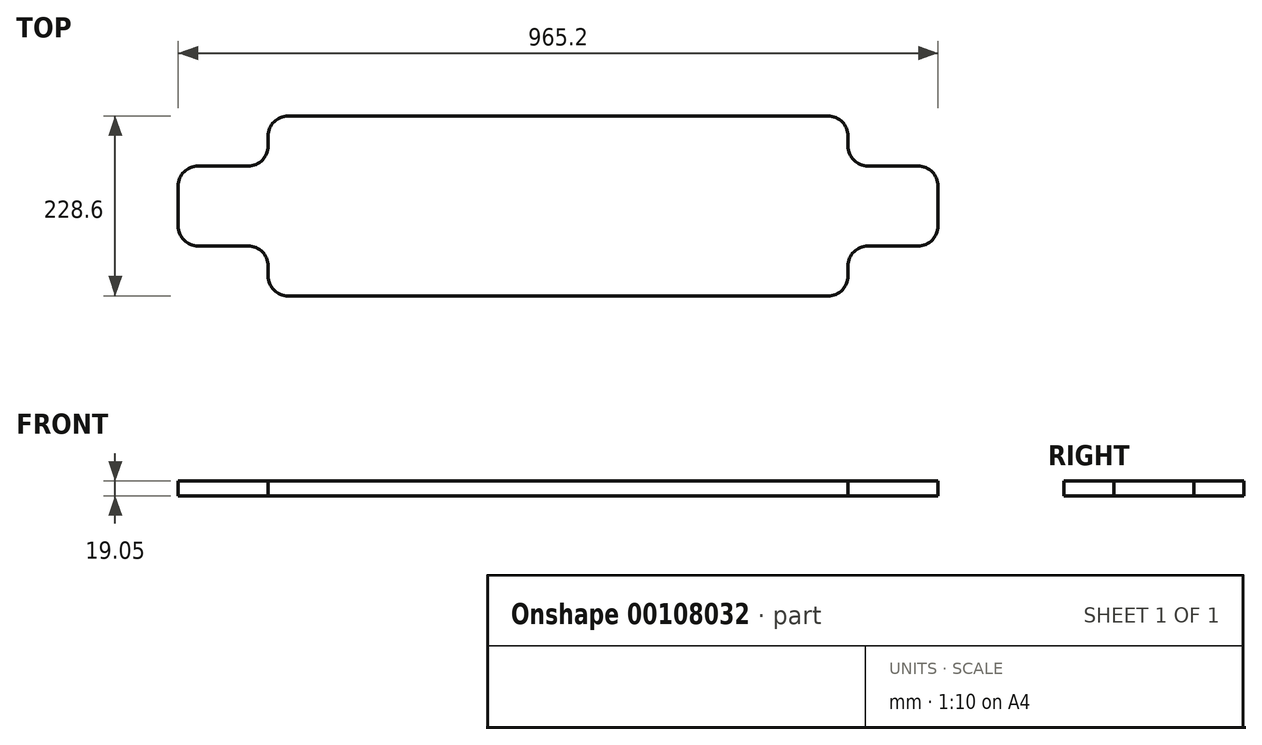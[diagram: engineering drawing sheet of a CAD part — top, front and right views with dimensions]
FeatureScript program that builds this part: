
annotation { "Feature Type Name" : "Feature", "Feature Type Description" : "" }
export const myFeature = defineFeature(function(context is Context, id is Id, definition is map)
    precondition{}
    {
        {
            var Q0;
            Q0=qCreatedBy(makeId("Top.planeOp"),FACE);
            var sketch = newSketch(context, id + "F0", { "sketchPlane" : qUnion([Q0])});
            skLineSegment(sketch, "E0", {"start": v(-342.9, 114.3) * mm, "end": v(342.9, 114.3) * mm});
            skLineSegment(sketch, "E1", {"start": v(368.3, 88.9) * mm, "end": v(368.3, 76.2) * mm});
            skLineSegment(sketch, "E2", {"start": v(393.7, 50.8) * mm, "end": v(457.2, 50.8) * mm});
            skLineSegment(sketch, "E3", {"start": v(482.6, 25.4) * mm, "end": v(482.6, -25.4) * mm});
            skLineSegment(sketch, "E4", {"start": v(457.2, -50.8) * mm, "end": v(393.7, -50.8) * mm});
            skLineSegment(sketch, "E5", {"start": v(368.3, -76.2) * mm, "end": v(368.3, -88.9) * mm});
            skLineSegment(sketch, "E6", {"start": v(342.9, -114.3) * mm, "end": v(-342.9, -114.3) * mm});
            skLineSegment(sketch, "E7", {"start": v(-368.3, -88.9) * mm, "end": v(-368.3, -76.2) * mm});
            skLineSegment(sketch, "E8", {"start": v(-393.7, -50.8) * mm, "end": v(-457.2, -50.8) * mm});
            skLineSegment(sketch, "E9", {"start": v(-482.6, -25.4) * mm, "end": v(-482.6, 25.4) * mm});
            skLineSegment(sketch, "E10", {"start": v(-457.2, 50.8) * mm, "end": v(-393.7, 50.8) * mm});
            skLineSegment(sketch, "E11", {"start": v(-368.3, 76.2) * mm, "end": v(-368.3, 88.9) * mm});
            skLineSegment(sketch, "E12", {"start": v(-368.3, 114.3) * mm, "end": v(368.3, -114.3) * mm, "construction": true});
            skPoint(sketch, "E13", {"position": v(0, 0) * mm});
            skPoint(sketch, "E14.visualSharp", {"position": v(-368.3, 50.8) * mm});
            skArc(sketch, "E14.filletArc", {"start": v(-393.7, 50.8) * mm, "mid": v(-375.74, 58.24) * mm, "end": v(-368.3, 76.2) * mm});
            skPoint(sketch, "E15.visualSharp", {"position": v(-482.6, 50.8) * mm});
            skArc(sketch, "E15.filletArc", {"start": v(-457.2, 50.8) * mm, "mid": v(-475.16, 43.36) * mm, "end": v(-482.6, 25.4) * mm});
            skPoint(sketch, "E16.visualSharp", {"position": v(-482.6, -50.8) * mm});
            skArc(sketch, "E16.filletArc", {"start": v(-482.6, -25.4) * mm, "mid": v(-475.16, -43.36) * mm, "end": v(-457.2, -50.8) * mm});
            skPoint(sketch, "E17.visualSharp", {"position": v(-368.3, -50.8) * mm});
            skArc(sketch, "E17.filletArc", {"start": v(-368.3, -76.2) * mm, "mid": v(-375.74, -58.24) * mm, "end": v(-393.7, -50.8) * mm});
            skPoint(sketch, "E18.visualSharp", {"position": v(-368.3, -114.3) * mm});
            skArc(sketch, "E18.filletArc", {"start": v(-368.3, -88.9) * mm, "mid": v(-360.86, -106.86) * mm, "end": v(-342.9, -114.3) * mm});
            skPoint(sketch, "E19.visualSharp", {"position": v(-368.3, 114.3) * mm});
            skArc(sketch, "E19.filletArc", {"start": v(-342.9, 114.3) * mm, "mid": v(-360.86, 106.86) * mm, "end": v(-368.3, 88.9) * mm});
            skPoint(sketch, "E20.visualSharp", {"position": v(368.3, -114.3) * mm});
            skArc(sketch, "E20.filletArc", {"start": v(342.9, -114.3) * mm, "mid": v(360.86, -106.86) * mm, "end": v(368.3, -88.9) * mm});
            skPoint(sketch, "E21.visualSharp", {"position": v(368.3, -50.8) * mm});
            skArc(sketch, "E21.filletArc", {"start": v(393.7, -50.8) * mm, "mid": v(375.74, -58.24) * mm, "end": v(368.3, -76.2) * mm});
            skPoint(sketch, "E22.visualSharp", {"position": v(482.6, -50.8) * mm});
            skArc(sketch, "E22.filletArc", {"start": v(457.2, -50.8) * mm, "mid": v(475.16, -43.36) * mm, "end": v(482.6, -25.4) * mm});
            skPoint(sketch, "E23.visualSharp", {"position": v(482.6, 50.8) * mm});
            skArc(sketch, "E23.filletArc", {"start": v(482.6, 25.4) * mm, "mid": v(475.16, 43.36) * mm, "end": v(457.2, 50.8) * mm});
            skPoint(sketch, "E24.visualSharp", {"position": v(368.3, 50.8) * mm});
            skArc(sketch, "E24.filletArc", {"start": v(368.3, 76.2) * mm, "mid": v(375.74, 58.24) * mm, "end": v(393.7, 50.8) * mm});
            skPoint(sketch, "E25.visualSharp", {"position": v(368.3, 114.3) * mm});
            skArc(sketch, "E25.filletArc", {"start": v(368.3, 88.9) * mm, "mid": v(360.86, 106.86) * mm, "end": v(342.9, 114.3) * mm});
            skLineSegment(sketch, "E26", {"start": v(-292.1, 114.3) * mm, "end": v(-292.1, 63.5) * mm});
            skLineSegment(sketch, "E27", {"start": v(-292.1, 63.5) * mm, "end": v(-292.1, -63.5) * mm});
            skLineSegment(sketch, "E28", {"start": v(-292.1, -63.5) * mm, "end": v(-292.1, -114.3) * mm});
            skLineSegment(sketch, "E29", {"start": v(292.1, 114.3) * mm, "end": v(292.1, 63.5) * mm});
            skLineSegment(sketch, "E30", {"start": v(292.1, 63.5) * mm, "end": v(292.1, -63.5) * mm});
            skLineSegment(sketch, "E31", {"start": v(292.1, -63.5) * mm, "end": v(292.1, -114.3) * mm});
            skLineSegment(sketch, "E32", {"start": v(-88.9, 114.3) * mm, "end": v(-88.9, 0) * mm});
            skLineSegment(sketch, "E33", {"start": v(-88.9, 0) * mm, "end": v(-88.9, -114.3) * mm});
            skLineSegment(sketch, "E34", {"start": v(88.9, 114.3) * mm, "end": v(88.9, 0) * mm});
            skLineSegment(sketch, "E35", {"start": v(88.9, 0) * mm, "end": v(88.9, -114.3) * mm});
            skSolve(sketch);
        }
        {
            var Q0;
            Q0 = qSketchRegion(id + "F0", true);
            extrude(context, id + "F1", {"entities" : qUnion([Q0]), "depth" : 19.05 * mm});
        }
    });
